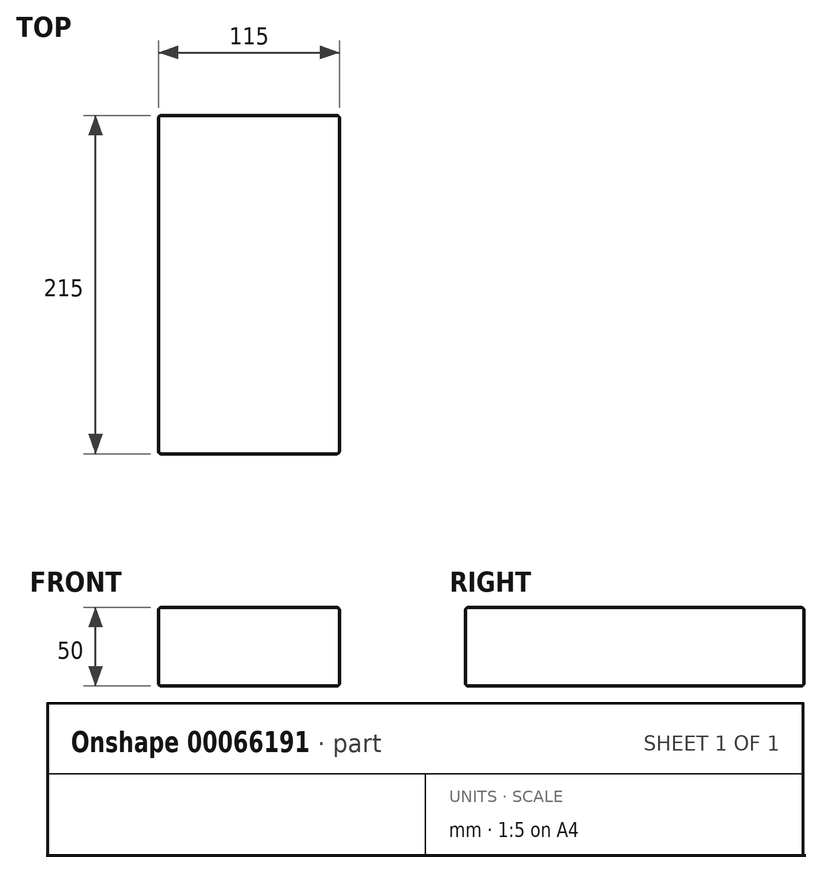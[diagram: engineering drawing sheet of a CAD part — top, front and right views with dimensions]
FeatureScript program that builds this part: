
annotation { "Feature Type Name" : "Feature", "Feature Type Description" : "" }
export const myFeature = defineFeature(function(context is Context, id is Id, definition is map)
    precondition{}
    {
        {
            var Q0;
            Q0=qCreatedBy(makeId("Top.planeOp"),FACE);
            var sketch = newSketch(context, id + "F0", { "sketchPlane" : qUnion([Q0])});
            skLineSegment(sketch, "E0.bottom", {"start": v(0, 0) * mm, "end": v(-115, 0) * mm});
            skLineSegment(sketch, "E0.top", {"start": v(0, -215) * mm, "end": v(-115, -215) * mm});
            skLineSegment(sketch, "E0.left", {"start": v(0, 0) * mm, "end": v(0, -215) * mm});
            skLineSegment(sketch, "E0.right", {"start": v(-115, 0) * mm, "end": v(-115, -215) * mm});
            skSolve(sketch);
        }
        {
            var Q0;
            Q0=makeQuery(id+"F0.imprint","IMPRINT",FACE,{"disambiguationData":[TD([[makeQuery(id+"F0.imprint","IMPRINT",EDGE,{"derivedFrom":sQuery(id+"F0.wireOp",EDGE,"E0.bottom")}),1.0]])]});
            extrude(context, id + "F1", {"entities" : qUnion([Q0]), "depth" : 50 * mm});
        }
        {
            var Q0;
            Q0=makeQuery(id+"F1.opExtrude","CAP_FACE",FACE,{"disambiguationData":[OSD([sQuery(id+"F0.wireOp",EDGE,"E0.bottom"),sQuery(id+"F0.wireOp",EDGE,"E0.top"),sQuery(id+"F0.wireOp",EDGE,"E0.left"),sQuery(id+"F0.wireOp",EDGE,"E0.right")])],"isStart":false});
            var Q1;
            Q1=makeQuery(id+"F1.opExtrude","SWEPT_FACE",FACE,{"disambiguationData":[OSD([sQuery(id+"F0.wireOp",EDGE,"E0.top")])]});
            var Q2;
            Q2=makeQuery(id+"F1.opExtrude","SWEPT_FACE",FACE,{"disambiguationData":[OSD([sQuery(id+"F0.wireOp",EDGE,"E0.left")])]});
            var Q3;
            Q3=makeQuery(id+"F1.opExtrude","CAP_FACE",FACE,{"disambiguationData":[OSD([sQuery(id+"F0.wireOp",EDGE,"E0.bottom"),sQuery(id+"F0.wireOp",EDGE,"E0.top"),sQuery(id+"F0.wireOp",EDGE,"E0.left"),sQuery(id+"F0.wireOp",EDGE,"E0.right")])],"isStart":true});
            var Q4;
            Q4=makeQuery(id+"F1.opExtrude","SWEPT_FACE",FACE,{"disambiguationData":[OSD([sQuery(id+"F0.wireOp",EDGE,"E0.right")])]});
            var Q5;
            Q5=makeQuery(id+"F1.opExtrude","SWEPT_FACE",FACE,{"disambiguationData":[OSD([sQuery(id+"F0.wireOp",EDGE,"E0.bottom")])]});
            fillet(context, id + "F2", {"entities" : qUnion([Q0, Q1, Q2, Q3, Q4, Q5]), "radius" : 2 * mm, "tangentPropagation" : true, "allowEdgeOverflow" : false});
        }
    });
